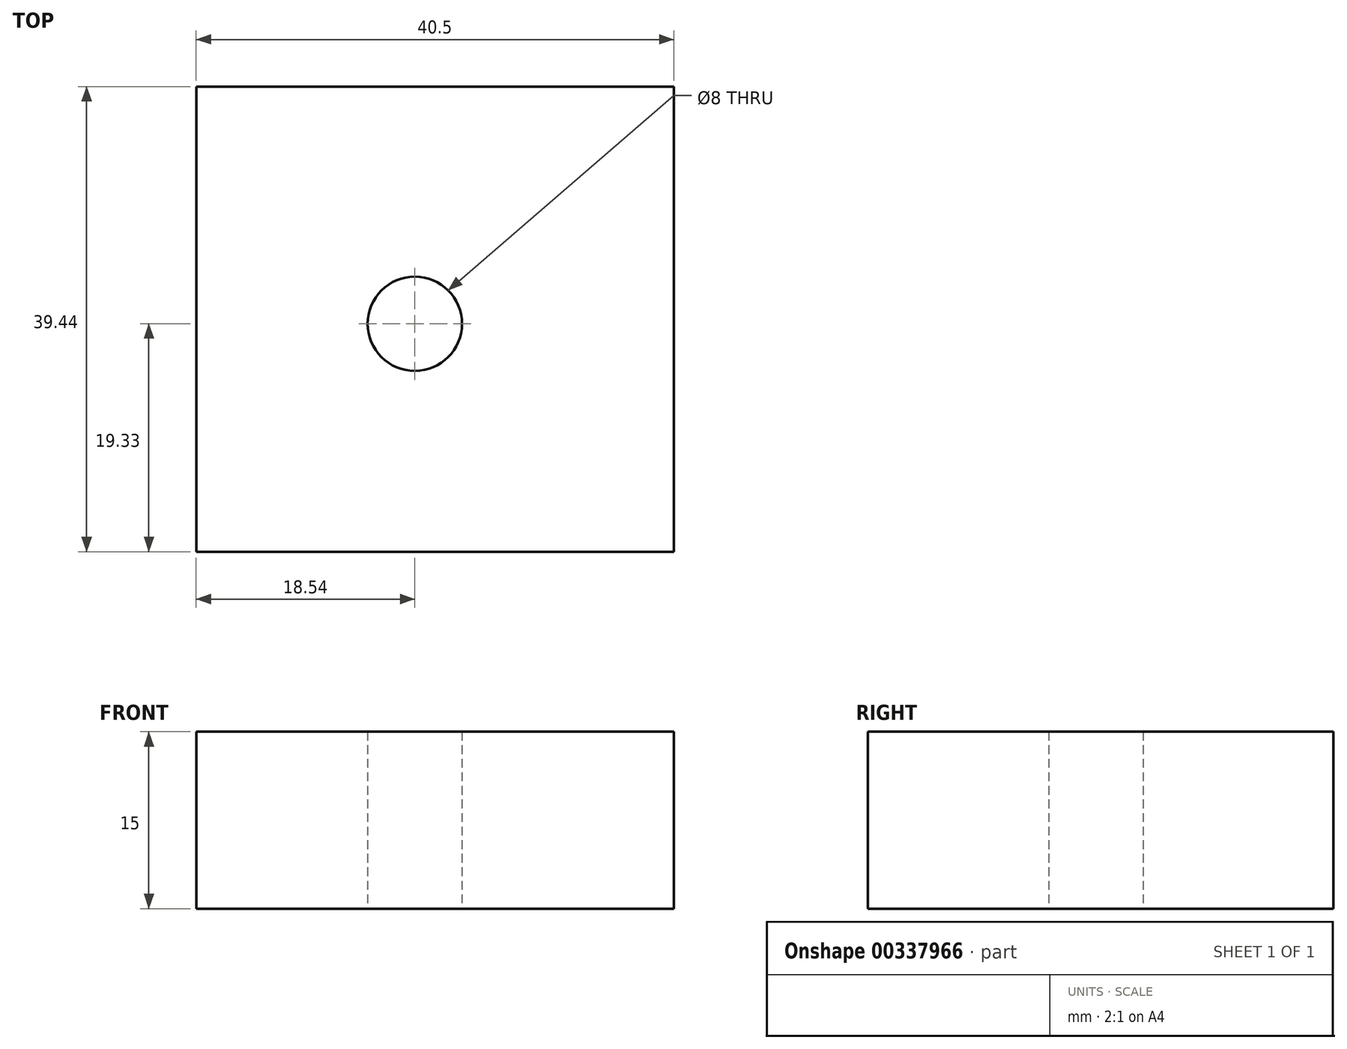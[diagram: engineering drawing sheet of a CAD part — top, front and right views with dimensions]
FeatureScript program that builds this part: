
annotation { "Feature Type Name" : "Feature", "Feature Type Description" : "" }
export const myFeature = defineFeature(function(context is Context, id is Id, definition is map)
    precondition{}
    {
        {
            var Q0;
            Q0=qCreatedBy(makeId("Top.planeOp"),FACE);
            var sketch = newSketch(context, id + "F0", { "sketchPlane" : qUnion([Q0])});
            skCircle(sketch, "E0", {"center": v(0, 0) * mm, "radius": 4 * mm});
            skLineSegment(sketch, "E1.bottom", {"start": v(-18.54, 20.11) * mm, "end": v(21.96, 20.11) * mm});
            skLineSegment(sketch, "E1.top", {"start": v(-18.54, -19.33) * mm, "end": v(21.96, -19.33) * mm});
            skLineSegment(sketch, "E1.left", {"start": v(-18.54, 20.11) * mm, "end": v(-18.54, -19.33) * mm});
            skLineSegment(sketch, "E1.right", {"start": v(21.96, 20.11) * mm, "end": v(21.96, -19.33) * mm});
            skSolve(sketch);
        }
        {
            var Q0;
            Q0 = qSketchRegion(id + "F0", true);
            extrude(context, id + "F1", {"entities" : qUnion([Q0]), "depth" : 15 * mm});
        }
    });
